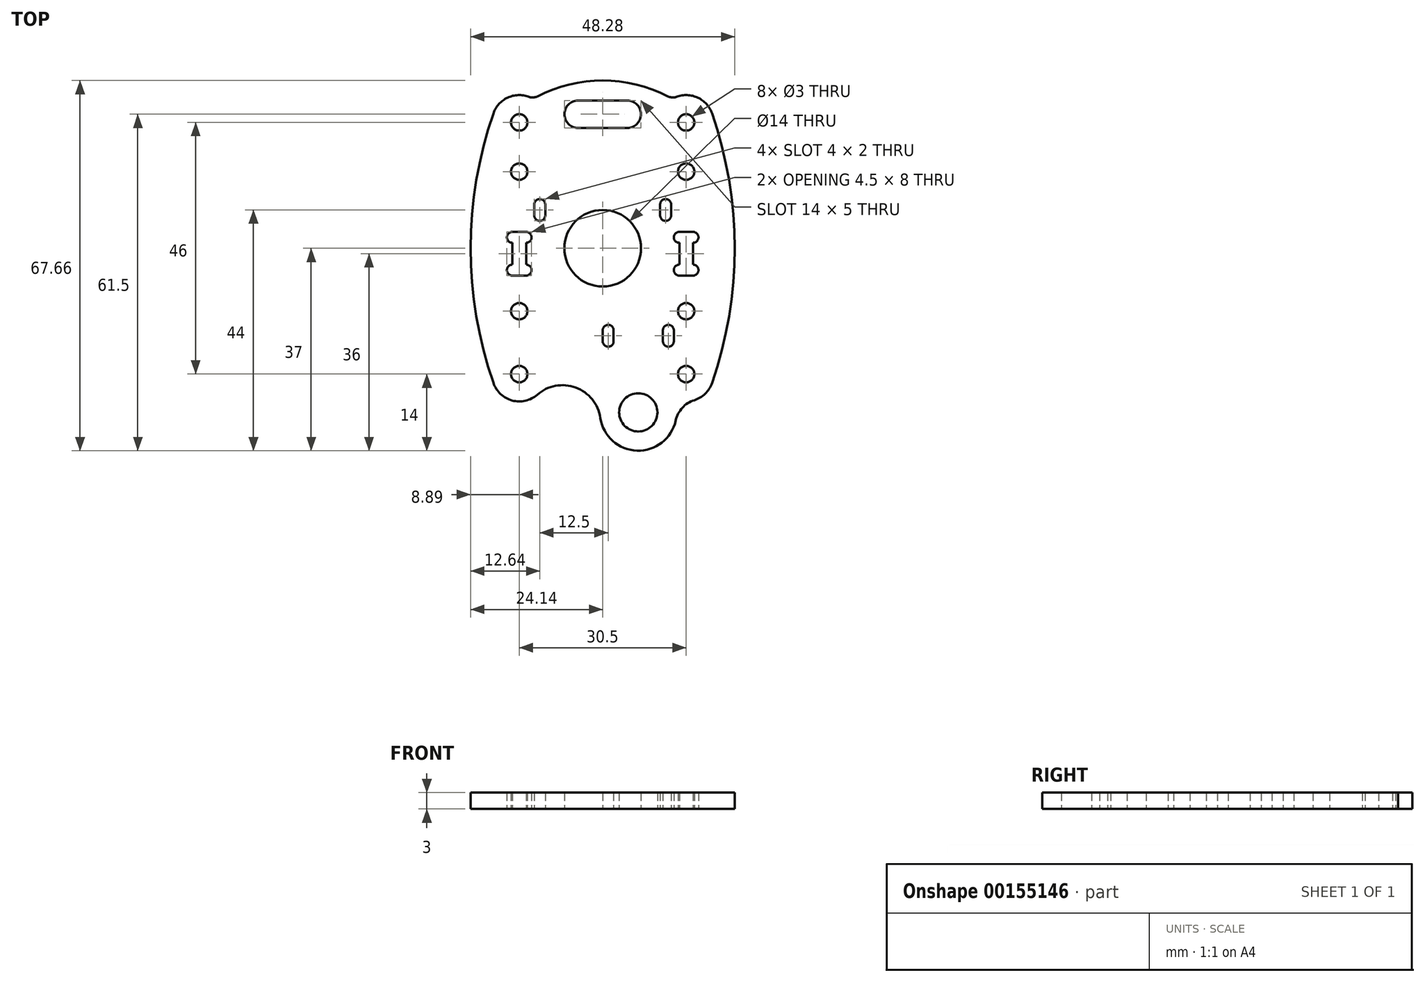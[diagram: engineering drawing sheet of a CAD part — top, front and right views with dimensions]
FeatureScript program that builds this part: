
annotation { "Feature Type Name" : "Feature", "Feature Type Description" : "" }
export const myFeature = defineFeature(function(context is Context, id is Id, definition is map)
    precondition{}
    {
        {
            var Q0;
            Q0=qCreatedBy(makeId("Top.planeOp"),FACE);
            var sketch = newSketch(context, id + "F0", { "sketchPlane" : qUnion([Q0])});
            skCircle(sketch, "E0", {"center": v(-15.25, 23) * mm, "radius": 1.5 * mm});
            skCircle(sketch, "E1.0.1.0", {"center": v(-15.25, -23) * mm, "radius": 1.5 * mm});
            skCircle(sketch, "E1.1.0.0", {"center": v(15.25, 23) * mm, "radius": 1.5 * mm});
            skCircle(sketch, "E1.1.1.0", {"center": v(15.25, -23) * mm, "radius": 1.5 * mm});
            skLineSegment(sketch, "E1.direction1", {"start": v(-15.25, 23) * mm, "end": v(15.25, 23) * mm, "construction": true});
            skLineSegment(sketch, "E1.direction2", {"start": v(-15.25, 23) * mm, "end": v(-15.25, -23) * mm, "construction": true});
            skArc(sketch, "E2", {"start": v(-13.5, 27.69) * mm, "mid": v(-17.38, 27.52) * mm, "end": v(-19.97, 24.64) * mm});
            skArc(sketch, "E3", {"start": v(19.97, 24.64) * mm, "mid": v(17.38, 27.52) * mm, "end": v(13.5, 27.69) * mm});
            skArc(sketch, "E4", {"start": v(-19.97, -24.64) * mm, "mid": v(-16.53, -27.83) * mm, "end": v(-11.96, -26.76) * mm});
            skArc(sketch, "E5", {"start": v(16.74, -27.77) * mm, "mid": v(18.73, -26.6) * mm, "end": v(19.97, -24.64) * mm});
            skCircle(sketch, "E6", {"center": v(-15.25, 14) * mm, "radius": 1.5 * mm});
            skCircle(sketch, "E7.0.1.0", {"center": v(-15.25, -11.5) * mm, "radius": 1.5 * mm});
            skCircle(sketch, "E7.1.0.0", {"center": v(15.25, 14) * mm, "radius": 1.5 * mm});
            skCircle(sketch, "E7.1.1.0", {"center": v(15.25, -11.5) * mm, "radius": 1.5 * mm});
            skLineSegment(sketch, "E7.direction1", {"start": v(-15.25, 14) * mm, "end": v(15.25, 14) * mm, "construction": true});
            skLineSegment(sketch, "E7.direction2", {"start": v(-15.25, 14) * mm, "end": v(-15.25, -11.5) * mm, "construction": true});
            skArc(sketch, "E8", {"start": v(-19.97, 24.64) * mm, "mid": v(-24.14, 0) * mm, "end": v(-19.97, -24.64) * mm});
            skArc(sketch, "E9", {"start": v(19.97, -24.64) * mm, "mid": v(24.14, 0) * mm, "end": v(19.97, 24.64) * mm});
            skCircle(sketch, "E10", {"center": v(6.5, -30) * mm, "radius": 3.5 * mm});
            skArc(sketch, "E11", {"start": v(-0.43, -31.02) * mm, "mid": v(6.26, -37) * mm, "end": v(13.34, -31.49) * mm});
            skArc(sketch, "E12", {"start": v(16.74, -27.77) * mm, "mid": v(14.54, -29.17) * mm, "end": v(13.34, -31.49) * mm});
            skArc(sketch, "E13", {"start": v(-0.43, -31.02) * mm, "mid": v(-4.93, -25.47) * mm, "end": v(-11.96, -26.76) * mm});
            skLineSegment(sketch, "E14.bottom", {"start": v(0, -15) * mm, "end": v(2, -15) * mm, "construction": true});
            skLineSegment(sketch, "E14.top", {"start": v(0, -17) * mm, "end": v(2, -17) * mm, "construction": true});
            skLineSegment(sketch, "E14.left", {"start": v(0, -15) * mm, "end": v(0, -17) * mm});
            skLineSegment(sketch, "E14.right", {"start": v(2, -15) * mm, "end": v(2, -17) * mm});
            skLineSegment(sketch, "E15.bottom", {"start": v(11, -15) * mm, "end": v(13, -15) * mm, "construction": true});
            skLineSegment(sketch, "E15.top", {"start": v(11, -17) * mm, "end": v(13, -17) * mm, "construction": true});
            skLineSegment(sketch, "E15.left", {"start": v(11, -15) * mm, "end": v(11, -17) * mm});
            skLineSegment(sketch, "E15.right", {"start": v(13, -15) * mm, "end": v(13, -17) * mm});
            skArc(sketch, "E16", {"start": v(0, -17) * mm, "mid": v(1, -18) * mm, "end": v(2, -17) * mm});
            skArc(sketch, "E17", {"start": v(2, -15) * mm, "mid": v(1, -14) * mm, "end": v(0, -15) * mm});
            skArc(sketch, "E18", {"start": v(13, -15) * mm, "mid": v(12, -14) * mm, "end": v(11, -15) * mm});
            skArc(sketch, "E19", {"start": v(11, -17) * mm, "mid": v(12, -18) * mm, "end": v(13, -17) * mm});
            skCircle(sketch, "E20", {"center": v(0, 0) * mm, "radius": 7 * mm});
            skLineSegment(sketch, "E21.bottom", {"start": v(-12.5, 8) * mm, "end": v(-10.5, 8) * mm, "construction": true});
            skLineSegment(sketch, "E21.top", {"start": v(-12.5, 6) * mm, "end": v(-10.5, 6) * mm, "construction": true});
            skLineSegment(sketch, "E21.left", {"start": v(-12.5, 8) * mm, "end": v(-12.5, 6) * mm});
            skLineSegment(sketch, "E21.right", {"start": v(-10.5, 8) * mm, "end": v(-10.5, 6) * mm});
            skLineSegment(sketch, "E22.bottom", {"start": v(10.5, 8) * mm, "end": v(12.5, 8) * mm, "construction": true});
            skLineSegment(sketch, "E22.top", {"start": v(10.5, 6) * mm, "end": v(12.5, 6) * mm, "construction": true});
            skLineSegment(sketch, "E22.left", {"start": v(10.5, 8) * mm, "end": v(10.5, 6) * mm});
            skLineSegment(sketch, "E22.right", {"start": v(12.5, 8) * mm, "end": v(12.5, 6) * mm});
            skArc(sketch, "E23", {"start": v(-10.5, 8) * mm, "mid": v(-11.5, 9) * mm, "end": v(-12.5, 8) * mm});
            skArc(sketch, "E24", {"start": v(-12.5, 6) * mm, "mid": v(-11.5, 5) * mm, "end": v(-10.5, 6) * mm});
            skArc(sketch, "E25", {"start": v(12.5, 8) * mm, "mid": v(11.5, 9) * mm, "end": v(10.5, 8) * mm});
            skArc(sketch, "E26", {"start": v(10.5, 6) * mm, "mid": v(11.5, 5) * mm, "end": v(12.5, 6) * mm});
            skLineSegment(sketch, "E27.left", {"start": v(-14, -3) * mm, "end": v(-14, 1) * mm});
            skLineSegment(sketch, "E27.right", {"start": v(-16.5, -3) * mm, "end": v(-16.5, 1) * mm});
            skLineSegment(sketch, "E28.bottom", {"start": v(-16.5, -5) * mm, "end": v(-14, -5) * mm});
            skLineSegment(sketch, "E29.bottom", {"start": v(-14, 3) * mm, "end": v(-16.5, 3) * mm});
            skLineSegment(sketch, "E30", {"start": v(-16.5, -3) * mm, "end": v(-14, -3) * mm, "construction": true});
            skLineSegment(sketch, "E31", {"start": v(-16.5, 1) * mm, "end": v(-14, 1) * mm, "construction": true});
            skLineSegment(sketch, "E32", {"start": v(-16.5, -3) * mm, "end": v(-16.5, -5) * mm, "construction": true});
            skLineSegment(sketch, "E33", {"start": v(-14, -3) * mm, "end": v(-14, -5) * mm, "construction": true});
            skLineSegment(sketch, "E34", {"start": v(-16.5, 1) * mm, "end": v(-16.5, 3) * mm, "construction": true});
            skLineSegment(sketch, "E35", {"start": v(-14, 1) * mm, "end": v(-14, 3) * mm, "construction": true});
            skArc(sketch, "E36", {"start": v(-16.5, -3) * mm, "mid": v(-17.5, -4) * mm, "end": v(-16.5, -5) * mm});
            skArc(sketch, "E37", {"start": v(-14, -5) * mm, "mid": v(-13, -4) * mm, "end": v(-14, -3) * mm});
            skArc(sketch, "E38", {"start": v(-14, 1) * mm, "mid": v(-13, 2) * mm, "end": v(-14, 3) * mm});
            skArc(sketch, "E39", {"start": v(-16.5, 3) * mm, "mid": v(-17.5, 2) * mm, "end": v(-16.5, 1) * mm});
            skLineSegment(sketch, "E40.MirrorCS", {"start": v(14, 1) * mm, "end": v(14, 3) * mm, "construction": true});
            skLineSegment(sketch, "E41.MirrorCS", {"start": v(16.5, -3) * mm, "end": v(16.5, -5) * mm, "construction": true});
            skLineSegment(sketch, "E42.MirrorCS", {"start": v(16.5, 1) * mm, "end": v(16.5, 3) * mm, "construction": true});
            skLineSegment(sketch, "E43.MirrorCS", {"start": v(14, -3) * mm, "end": v(14, -5) * mm, "construction": true});
            skArc(sketch, "E44.MirrorCS", {"start": v(16.5, 3) * mm, "mid": v(17.5, 2) * mm, "end": v(16.5, 1) * mm});
            skLineSegment(sketch, "E45.MirrorCS", {"start": v(16.5, -3) * mm, "end": v(14, -3) * mm, "construction": true});
            skArc(sketch, "E46.MirrorCS", {"start": v(14, 1) * mm, "mid": v(13, 2) * mm, "end": v(14, 3) * mm});
            skArc(sketch, "E47.MirrorCS", {"start": v(14, -5) * mm, "mid": v(13, -4) * mm, "end": v(14, -3) * mm});
            skLineSegment(sketch, "E48.MirrorCS", {"start": v(16.5, -5) * mm, "end": v(14, -5) * mm});
            skArc(sketch, "E49.MirrorCS", {"start": v(16.5, -3) * mm, "mid": v(17.5, -4) * mm, "end": v(16.5, -5) * mm});
            skLineSegment(sketch, "E50.MirrorCS", {"start": v(14, -3) * mm, "end": v(14, 1) * mm});
            skLineSegment(sketch, "E51.MirrorCS", {"start": v(14, 3) * mm, "end": v(16.5, 3) * mm});
            skLineSegment(sketch, "E52.MirrorCS", {"start": v(16.5, -3) * mm, "end": v(16.5, 1) * mm});
            skLineSegment(sketch, "E53.MirrorCS", {"start": v(16.5, 1) * mm, "end": v(14, 1) * mm, "construction": true});
            skLineSegment(sketch, "E54.bottom", {"start": v(-4.5, 27) * mm, "end": v(4.5, 27) * mm});
            skLineSegment(sketch, "E54.top", {"start": v(-4.5, 22) * mm, "end": v(4.5, 22) * mm});
            skLineSegment(sketch, "E54.left", {"start": v(-4.5, 27) * mm, "end": v(-4.5, 22) * mm, "construction": true});
            skLineSegment(sketch, "E54.right", {"start": v(4.5, 27) * mm, "end": v(4.5, 22) * mm, "construction": true});
            skArc(sketch, "E55", {"start": v(4.5, 22) * mm, "mid": v(7, 24.5) * mm, "end": v(4.5, 27) * mm});
            skArc(sketch, "E56", {"start": v(-4.5, 27) * mm, "mid": v(-7, 24.5) * mm, "end": v(-4.5, 22) * mm});
            skArc(sketch, "E57", {"start": v(11.9, 27.78) * mm, "mid": v(0, 30.66) * mm, "end": v(-11.9, 27.78) * mm});
            skLineSegment(sketch, "E58", {"start": v(0, 0) * mm, "end": v(-12.74, 27.33) * mm, "construction": true});
            skLineSegment(sketch, "E59", {"start": v(0, 0) * mm, "end": v(12.74, 27.33) * mm, "construction": true});
            skPoint(sketch, "E60.visualSharp", {"position": v(-12.74, 27.33) * mm});
            skArc(sketch, "E60.filletArc", {"start": v(-13.5, 27.69) * mm, "mid": v(-12.69, 27.56) * mm, "end": v(-11.9, 27.78) * mm});
            skPoint(sketch, "E61.visualSharp", {"position": v(12.74, 27.33) * mm});
            skArc(sketch, "E61.filletArc", {"start": v(11.9, 27.78) * mm, "mid": v(12.69, 27.56) * mm, "end": v(13.5, 27.69) * mm});
            skSolve(sketch);
        }
        {
            var Q0;
            Q0=makeQuery(id+"F0.imprint","IMPRINT",FACE,{"disambiguationData":[TD([[makeQuery(id+"F0.imprint","IMPRINT",EDGE,{"derivedFrom":sQuery(id+"F0.wireOp",EDGE,"E0")}),-1.0]])]});
            extrude(context, id + "F1", {"entities" : qUnion([Q0]), "depth" : 3 * mm});
        }
    });
